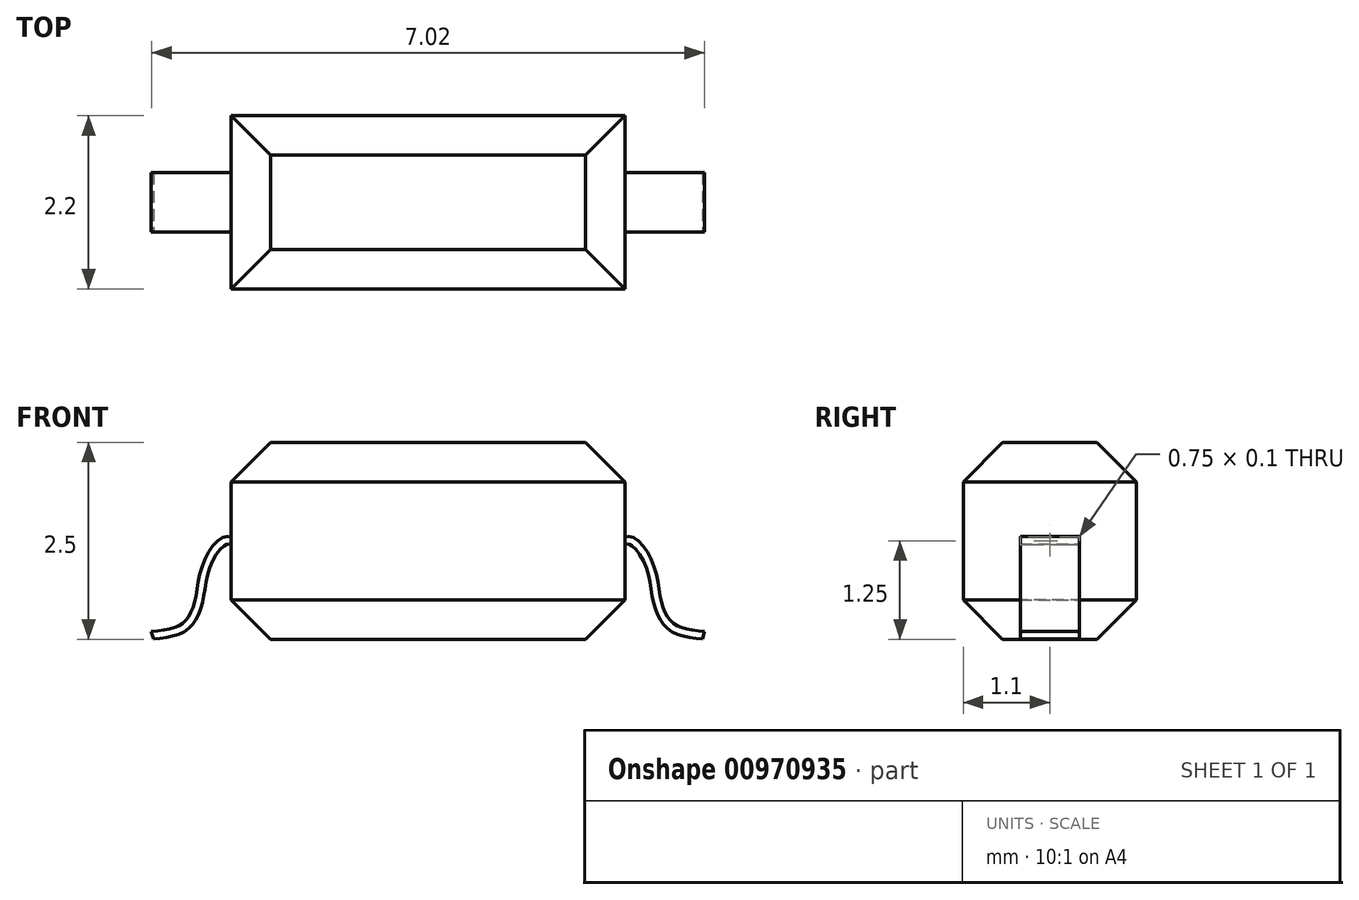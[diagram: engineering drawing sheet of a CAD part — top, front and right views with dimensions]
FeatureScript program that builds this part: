
annotation { "Feature Type Name" : "Feature", "Feature Type Description" : "" }
export const myFeature = defineFeature(function(context is Context, id is Id, definition is map)
    precondition{}
    {
        {
            var Q0;
            Q0=qCreatedBy(makeId("Top.planeOp"),FACE);
            var sketch = newSketch(context, id + "F0", { "sketchPlane" : qUnion([Q0])});
            skLineSegment(sketch, "E0.bottom", {"start": v(-2.5, 1.1) * mm, "end": v(2.5, 1.1) * mm});
            skLineSegment(sketch, "E0.top", {"start": v(-2.5, -1.1) * mm, "end": v(2.5, -1.1) * mm});
            skLineSegment(sketch, "E0.left", {"start": v(-2.5, 1.1) * mm, "end": v(-2.5, -1.1) * mm});
            skLineSegment(sketch, "E0.right", {"start": v(2.5, 1.1) * mm, "end": v(2.5, -1.1) * mm});
            skSolve(sketch);
        }
        {
            var Q0;
            Q0=makeQuery(id+"F0.imprint","IMPRINT",FACE,{"disambiguationData":[TD([[makeQuery(id+"F0.imprint","IMPRINT",EDGE,{"derivedFrom":sQuery(id+"F0.wireOp",EDGE,"E0.bottom")}),-1.0]])]});
            extrude(context, id + "F1", {"entities" : qUnion([Q0]), "depth" : 2.5 * mm, "offsetDistance" : 25 * mm});
        }
        {
            var Q0;
            Q0=makeQuery(id+"F1.opExtrude","SWEPT_FACE",FACE,{"disambiguationData":[OSD([sQuery(id+"F0.wireOp",EDGE,"E0.left")])]});
            var sketch = newSketch(context, id + "F2", { "sketchPlane" : qUnion([Q0])});
            skLineSegment(sketch, "E1", {"start": v(-1.1, 1.25) * mm, "end": v(1.1, 1.25) * mm, "construction": true});
            skLineSegment(sketch, "E2.bottom", {"start": v(-0.37, 1.3) * mm, "end": v(0.38, 1.3) * mm});
            skLineSegment(sketch, "E2.top", {"start": v(-0.37, 1.2) * mm, "end": v(0.38, 1.2) * mm});
            skLineSegment(sketch, "E2.left", {"start": v(-0.37, 1.3) * mm, "end": v(-0.37, 1.2) * mm});
            skLineSegment(sketch, "E2.right", {"start": v(0.38, 1.3) * mm, "end": v(0.38, 1.2) * mm});
            skSolve(sketch);
        }
        {
            var Q0;
            Q0=qCreatedBy(makeId("Front.planeOp"),FACE);
            var sketch = newSketch(context, id + "F3", { "sketchPlane" : qUnion([Q0])});
            skLineSegment(sketch, "E3", {"start": v(0, 0) * mm, "end": v(-3.5, 0) * mm, "construction": true});
            skLineSegment(sketch, "E4", {"start": v(-3.5, 0) * mm, "end": v(-3.5, 0.05) * mm, "construction": true});
            skLineSegment(sketch, "E5.0", {"start": v(-2.5, 2.5) * mm, "end": v(-2.5, 0) * mm, "construction": true});
            skFitSpline(sketch, "E6", {"points": [v(-3.5, 0.05) * mm, v(-3.19, 0.1) * mm, v(-3.02, 0.24) * mm, v(-2.9, 0.5) * mm, v(-2.81, 0.94) * mm, v(-2.6, 1.24) * mm, v(-2.5, 1.25) * mm], "startDerivative": vector(1.9, 0.2) * mm, "endDerivative": vector(0.93, -0.18) * mm});
            skSolve(sketch);
        }
        {
            var Q0;
            Q0=makeQuery(id+"F2.imprint","IMPRINT",FACE,{"disambiguationData":[TD([[makeQuery(id+"F2.imprint","IMPRINT",EDGE,{"derivedFrom":sQuery(id+"F2.wireOp",EDGE,"E2.bottom")}),-1.0]])]});
            var Q1;
            Q1=sQuery(id+"F3.wireOp",EDGE,"E6");
            sweep(context, id + "F4", {"operationType" : NewBodyOperationType.ADD, "profiles" : qUnion([Q0]), "path" : qUnion([Q1])});
        }
        {
            var Q0;
            Q0=makeQuery(id+"F1.opExtrude","SWEPT_BODY",BODY,{"disambiguationData":[OSD([sQuery(id+"F0.wireOp",EDGE,"E0.bottom"),sQuery(id+"F0.wireOp",EDGE,"E0.top"),sQuery(id+"F0.wireOp",EDGE,"E0.left"),sQuery(id+"F0.wireOp",EDGE,"E0.right")])]});
            var Q1;
            Q1=qCreatedBy(makeId("Right.planeOp"),FACE);
            mirror(context, id + "F5", {"operationType" : NewBodyOperationType.ADD, "entities" : qUnion([Q0]), "mirrorPlane" : qUnion([Q1])});
        }
        {
            var Q0;
            Q0=makeQuery(id+"F1.opExtrude","CAP_EDGE",EDGE,{"disambiguationData":[OSD([sQuery(id+"F0.wireOp",EDGE,"E0.left")])],"isStart":false});
            var Q1;
            Q1=makeQuery(id+"F1.opExtrude","CAP_EDGE",EDGE,{"disambiguationData":[OSD([sQuery(id+"F0.wireOp",EDGE,"E0.right")])],"isStart":false});
            var Q2;
            Q2=makeQuery(id+"F1.opExtrude","CAP_EDGE",EDGE,{"disambiguationData":[OSD([sQuery(id+"F0.wireOp",EDGE,"E0.top")])],"isStart":false});
            var Q3;
            Q3=makeQuery(id+"F1.opExtrude","CAP_EDGE",EDGE,{"disambiguationData":[OSD([sQuery(id+"F0.wireOp",EDGE,"E0.top")])],"isStart":true});
            var Q4;
            Q4=makeQuery(id+"F1.opExtrude","CAP_EDGE",EDGE,{"disambiguationData":[OSD([sQuery(id+"F0.wireOp",EDGE,"E0.bottom")])],"isStart":true});
            var Q5;
            Q5=makeQuery(id+"F1.opExtrude","CAP_EDGE",EDGE,{"disambiguationData":[OSD([sQuery(id+"F0.wireOp",EDGE,"E0.left")])],"isStart":true});
            var Q6;
            Q6=makeQuery(id+"F1.opExtrude","CAP_EDGE",EDGE,{"disambiguationData":[OSD([sQuery(id+"F0.wireOp",EDGE,"E0.right")])],"isStart":true});
            chamfer(context, id + "F6", {"entities" : qUnion([Q0, Q1, Q2, Q3, Q4, Q5, Q6]), "width" : 0.5 * mm, "tangentPropagation" : true});
        }
        {
            var Q0;
            Q0=makeQuery(id+"F1.opExtrude","CAP_EDGE",EDGE,{"disambiguationData":[OSD([sQuery(id+"F0.wireOp",EDGE,"E0.bottom")])],"isStart":false});
            chamfer(context, id + "F7", {"entities" : qUnion([Q0]), "width" : 0.5 * mm, "tangentPropagation" : true});
        }
    });
